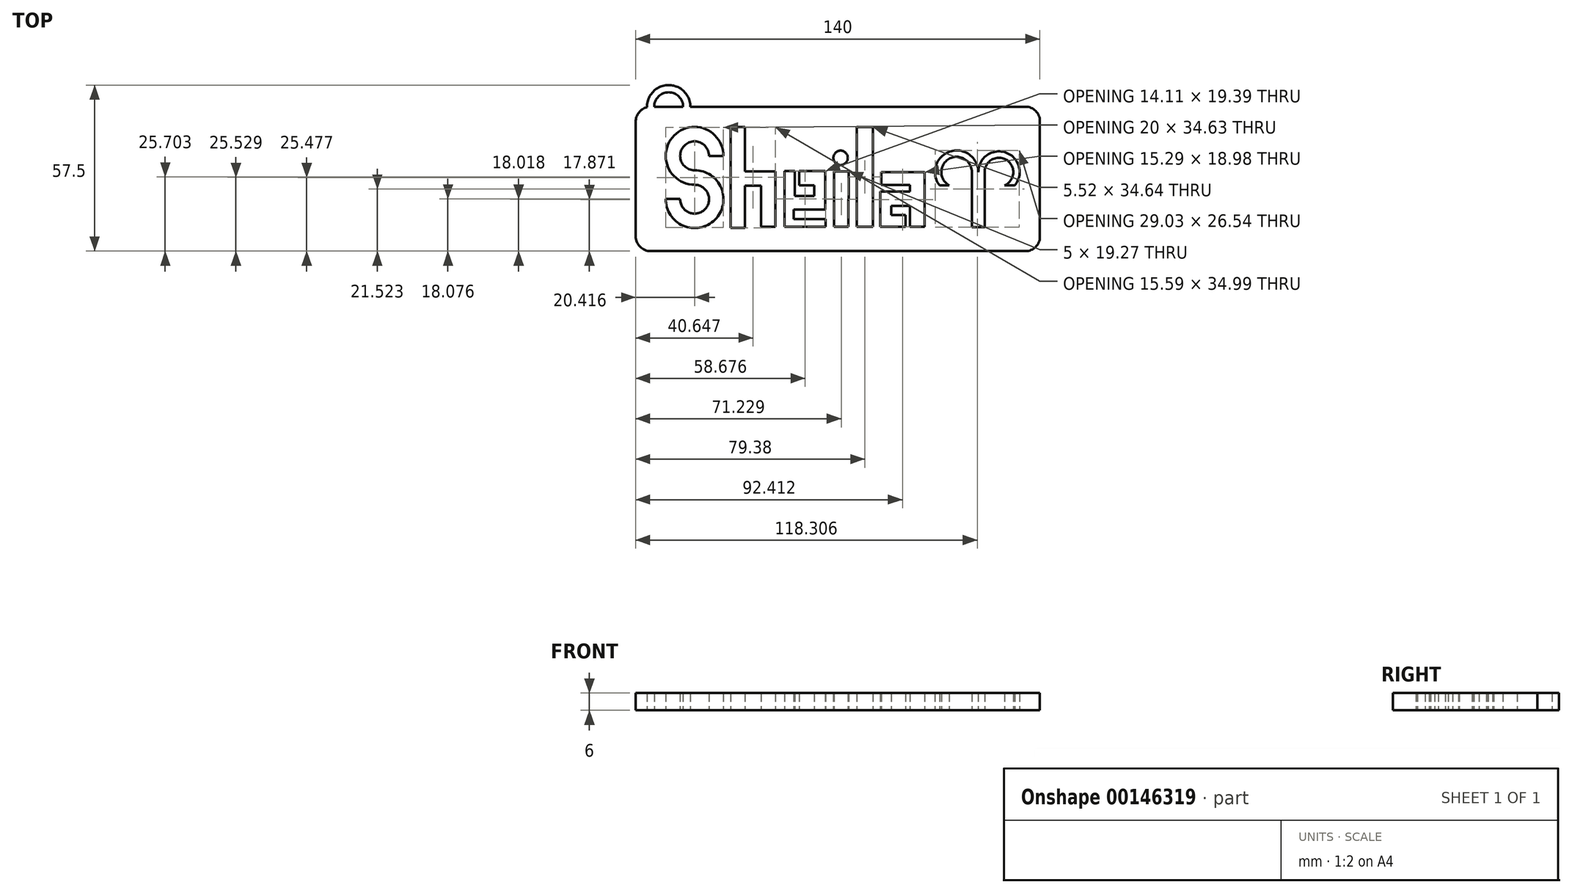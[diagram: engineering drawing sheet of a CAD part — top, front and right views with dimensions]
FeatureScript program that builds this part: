
annotation { "Feature Type Name" : "Feature", "Feature Type Description" : "" }
export const myFeature = defineFeature(function(context is Context, id is Id, definition is map)
    precondition{}
    {
        {
            var Q0;
            Q0=qCreatedBy(makeId("Top.planeOp"),FACE);
            var sketch = newSketch(context, id + "F0", { "sketchPlane" : qUnion([Q0])});
            skLineSegment(sketch, "E0.bottom", {"start": v(-68.38, 27.23) * mm, "end": v(61.38, 27.23) * mm});
            skLineSegment(sketch, "E0.top", {"start": v(-68.41, -22.77) * mm, "end": v(61.38, -22.77) * mm});
            skLineSegment(sketch, "E0.left", {"start": v(-73.62, 22) * mm, "end": v(-73.62, -17.56) * mm});
            skLineSegment(sketch, "E0.right", {"start": v(66.38, 22.23) * mm, "end": v(66.38, -17.77) * mm});
            skPoint(sketch, "E1.visualSharp", {"position": v(-73.62, 27.23) * mm});
            skArc(sketch, "E1.filletArc", {"start": v(-68.38, 27.23) * mm, "mid": v(-72.08, 25.7) * mm, "end": v(-73.62, 22) * mm});
            skPoint(sketch, "E2.visualSharp", {"position": v(-73.62, -22.77) * mm});
            skArc(sketch, "E2.filletArc", {"start": v(-73.62, -17.56) * mm, "mid": v(-72.1, -21.25) * mm, "end": v(-68.41, -22.77) * mm});
            skPoint(sketch, "E3.visualSharp", {"position": v(66.38, 27.23) * mm});
            skArc(sketch, "E3.filletArc", {"start": v(66.38, 22.23) * mm, "mid": v(64.92, 25.76) * mm, "end": v(61.38, 27.23) * mm});
            skPoint(sketch, "E4.visualSharp", {"position": v(66.38, -22.77) * mm});
            skArc(sketch, "E4.filletArc", {"start": v(61.38, -22.77) * mm, "mid": v(64.92, -21.3) * mm, "end": v(66.38, -17.77) * mm});
            skLineSegment(sketch, "E5", {"start": v(-58.07, -4.63) * mm, "end": v(-58.2, -4.63) * mm});
            skLineSegment(sketch, "E6", {"start": v(-40.77, 20.25) * mm, "end": v(-40.77, -14.74) * mm});
            skLineSegment(sketch, "E7.trimOffspring", {"start": v(-22, -14.39) * mm, "end": v(-7.9, -14.39) * mm});
            skLineSegment(sketch, "E8", {"start": v(-40.77, -14.74) * mm, "end": v(-35.77, -14.74) * mm});
            skLineSegment(sketch, "E9", {"start": v(-35.77, -14.74) * mm, "end": v(-35.77, -0.15) * mm});
            skLineSegment(sketch, "E10", {"start": v(-35.77, -0.15) * mm, "end": v(-30.2, -0.15) * mm});
            skLineSegment(sketch, "E11", {"start": v(-30.2, -0.15) * mm, "end": v(-30.2, -14.39) * mm});
            skLineSegment(sketch, "E12", {"start": v(-30.2, -14.39) * mm, "end": v(-25.18, -14.39) * mm});
            skLineSegment(sketch, "E13", {"start": v(-40.77, 20.25) * mm, "end": v(-35.77, 20.25) * mm});
            skLineSegment(sketch, "E14", {"start": v(-7.94, 5) * mm, "end": v(-22, 5) * mm});
            skLineSegment(sketch, "E15", {"start": v(-22, 5) * mm, "end": v(-22, -14.39) * mm});
            skLineSegment(sketch, "E16", {"start": v(-25.18, -14.39) * mm, "end": v(-25.18, 5.19) * mm});
            skLineSegment(sketch, "E17", {"start": v(-25.18, 4.88) * mm, "end": v(-35.77, 4.88) * mm});
            skLineSegment(sketch, "E18", {"start": v(-35.77, 4.88) * mm, "end": v(-35.77, 20.25) * mm});
            skLineSegment(sketch, "E19", {"start": v(-7.94, 5) * mm, "end": v(-7.94, -8.38) * mm});
            skLineSegment(sketch, "E20", {"start": v(-7.9, -14.39) * mm, "end": v(-7.9, -11.6) * mm});
            skLineSegment(sketch, "E21", {"start": v(-7.9, -11.6) * mm, "end": v(-18.85, -11.6) * mm});
            skLineSegment(sketch, "E22", {"start": v(-18.85, -11.6) * mm, "end": v(-18.85, -8.38) * mm});
            skLineSegment(sketch, "E23", {"start": v(-18.85, -8.38) * mm, "end": v(-7.94, -8.38) * mm});
            skLineSegment(sketch, "E24", {"start": v(-11.73, 0) * mm, "end": v(-11.73, -3.67) * mm});
            skLineSegment(sketch, "E25", {"start": v(-11.73, -3.67) * mm, "end": v(-18.48, -3.67) * mm});
            skLineSegment(sketch, "E26", {"start": v(-18.48, -3.67) * mm, "end": v(-18.48, 0) * mm});
            skLineSegment(sketch, "E27", {"start": v(-18.48, 0) * mm, "end": v(-11.73, 0) * mm});
            skLineSegment(sketch, "E28", {"start": v(-35.77, 4.88) * mm, "end": v(-25.18, 4.88) * mm});
            skLineSegment(sketch, "E29", {"start": v(-4.9, -14.39) * mm, "end": v(-4.9, 4.88) * mm});
            skLineSegment(sketch, "E30", {"start": v(-4.9, 4.88) * mm, "end": v(0.1, 4.87) * mm});
            skLineSegment(sketch, "E31", {"start": v(0.1, 4.87) * mm, "end": v(0, -14.39) * mm});
            skLineSegment(sketch, "E32", {"start": v(0, -14.39) * mm, "end": v(-4.9, -14.39) * mm});
            skLineSegment(sketch, "E33.trimOffspring", {"start": v(-4.9, -14.39) * mm, "end": v(0, -14.39) * mm});
            skCircle(sketch, "E34", {"center": v(-2.64, 9.53) * mm, "radius": 2.5 * mm});
            skLineSegment(sketch, "E35", {"start": v(3, 20.25) * mm, "end": v(3, -14.39) * mm});
            skLineSegment(sketch, "E36", {"start": v(3, -14.39) * mm, "end": v(8.52, -14.39) * mm});
            skLineSegment(sketch, "E37", {"start": v(8.52, -14.39) * mm, "end": v(8.52, 20.25) * mm});
            skLineSegment(sketch, "E38.trimOffspring", {"start": v(11.15, -14.39) * mm, "end": v(26.44, -14.39) * mm});
            skLineSegment(sketch, "E39", {"start": v(26.38, 4.6) * mm, "end": v(26.44, 4.6) * mm});
            skLineSegment(sketch, "E40", {"start": v(11.15, -14.39) * mm, "end": v(11.15, -2.12) * mm});
            skLineSegment(sketch, "E41", {"start": v(11.15, -2.12) * mm, "end": v(21.4, -2.12) * mm});
            skLineSegment(sketch, "E42", {"start": v(26.44, 4.6) * mm, "end": v(11.42, 4.6) * mm});
            skLineSegment(sketch, "E43", {"start": v(11.42, 4.6) * mm, "end": v(11.42, 0.12) * mm});
            skLineSegment(sketch, "E44", {"start": v(11.42, 0.12) * mm, "end": v(21.4, 0.12) * mm});
            skLineSegment(sketch, "E45", {"start": v(21.4, 0.12) * mm, "end": v(21.4, -2.2) * mm});
            skLineSegment(sketch, "E46", {"start": v(14.95, -7.12) * mm, "end": v(21.4, -7.12) * mm});
            skLineSegment(sketch, "E47", {"start": v(21.4, -7.12) * mm, "end": v(21.4, -10.27) * mm});
            skLineSegment(sketch, "E48", {"start": v(21.4, -10.27) * mm, "end": v(14.95, -10.27) * mm});
            skLineSegment(sketch, "E49", {"start": v(14.95, -10.27) * mm, "end": v(14.95, -7.12) * mm});
            skLineSegment(sketch, "E50", {"start": v(26.44, 4.6) * mm, "end": v(26.44, -14.39) * mm});
            skLineSegment(sketch, "E51", {"start": v(3, 20.25) * mm, "end": v(8.52, 20.25) * mm});
            skLineSegment(sketch, "E52.bottom", {"start": v(-65.84, 22.23) * mm, "end": v(58.88, 22.23) * mm});
            skLineSegment(sketch, "E52.top", {"start": v(-65.84, -17.77) * mm, "end": v(58.88, -17.77) * mm});
            skLineSegment(sketch, "E52.left", {"start": v(-68.34, 19.73) * mm, "end": v(-68.34, -15.27) * mm});
            skLineSegment(sketch, "E52.right", {"start": v(61.38, 19.73) * mm, "end": v(61.38, -15.27) * mm});
            skPoint(sketch, "E53.oppositeSnap0", {"position": v(-68.34, 2.23) * mm});
            skArc(sketch, "E54.filletArc", {"start": v(61.38, 19.73) * mm, "mid": v(60.65, 21.5) * mm, "end": v(58.88, 22.23) * mm});
            skArc(sketch, "E55.filletArc", {"start": v(58.88, -17.77) * mm, "mid": v(60.65, -17.04) * mm, "end": v(61.38, -15.27) * mm});
            skArc(sketch, "E56.filletArc", {"start": v(-65.84, 22.23) * mm, "mid": v(-67.6, 21.5) * mm, "end": v(-68.34, 19.73) * mm});
            skArc(sketch, "E57.filletArc", {"start": v(-68.34, -15.27) * mm, "mid": v(-67.6, -17.04) * mm, "end": v(-65.84, -17.77) * mm});
            skLineSegment(sketch, "E58.top", {"start": v(42.82, -14.52) * mm, "end": v(47.23, -14.52) * mm});
            skLineSegment(sketch, "E58.left", {"start": v(42.82, 4.6) * mm, "end": v(42.82, -14.52) * mm});
            skLineSegment(sketch, "E58.right", {"start": v(47.23, 4.6) * mm, "end": v(47.23, -14.52) * mm});
            skArc(sketch, "E59", {"start": v(45.04, 4.6) * mm, "mid": v(35.1, 11.7) * mm, "end": v(31.62, 0) * mm});
            skArc(sketch, "E60", {"start": v(42.82, 4.6) * mm, "mid": v(34.88, 9.16) * mm, "end": v(34.95, 0) * mm});
            skArc(sketch, "E61", {"start": v(54.09, 0) * mm, "mid": v(54.98, 8.73) * mm, "end": v(47.23, 4.6) * mm});
            skArc(sketch, "E62", {"start": v(57.7, 0) * mm, "mid": v(54.66, 11.34) * mm, "end": v(45.04, 4.6) * mm});
            skLineSegment(sketch, "E63", {"start": v(54.09, 0) * mm, "end": v(57.7, 0) * mm});
            skLineSegment(sketch, "E64", {"start": v(31.62, 0) * mm, "end": v(34.95, 0) * mm});
            skLineSegment(sketch, "E65.trimOffspring", {"start": v(-22, 4.88) * mm, "end": v(-7.94, 4.88) * mm});
            skArc(sketch, "E66", {"start": v(-54.68, 27.23) * mm, "mid": v(-62.26, 34.73) * mm, "end": v(-69.68, 27.07) * mm});
            skArc(sketch, "E67", {"start": v(-57.18, 27.23) * mm, "mid": v(-62.18, 32.23) * mm, "end": v(-67.18, 27.23) * mm});
            skLineSegment(sketch, "E68.bottom", {"start": v(-68.62, -22.77) * mm, "end": v(61.38, -22.77) * mm});
            skLineSegment(sketch, "E68.top", {"start": v(-68.62, 27.23) * mm, "end": v(61.38, 27.23) * mm});
            skLineSegment(sketch, "E68.left", {"start": v(-73.62, -17.77) * mm, "end": v(-73.62, 22.23) * mm});
            skLineSegment(sketch, "E68.right", {"start": v(66.38, -17.77) * mm, "end": v(66.38, 22.23) * mm});
            skArc(sketch, "E69.filletArc", {"start": v(-73.62, -17.77) * mm, "mid": v(-72.15, -21.3) * mm, "end": v(-68.62, -22.77) * mm});
            skArc(sketch, "E70.filletArc", {"start": v(-68.62, 27.23) * mm, "mid": v(-72.15, 25.76) * mm, "end": v(-73.62, 22.23) * mm});
            skArc(sketch, "E71", {"start": v(-43.2, 10.22) * mm, "mid": v(-60.28, 17.29) * mm, "end": v(-53.2, 0.22) * mm});
            skArc(sketch, "E72", {"start": v(-48.2, 10.22) * mm, "mid": v(-56.74, 13.75) * mm, "end": v(-53.2, 5.22) * mm});
            skArc(sketch, "E73", {"start": v(-58.2, -4.63) * mm, "mid": v(-49.72, -8.37) * mm, "end": v(-53.2, 0.22) * mm});
            skArc(sketch, "E74", {"start": v(-63.2, -4.63) * mm, "mid": v(-46.19, -11.9) * mm, "end": v(-53.2, 5.22) * mm});
            skLineSegment(sketch, "E75", {"start": v(-58.07, -4.63) * mm, "end": v(-63.2, -4.63) * mm});
            skLineSegment(sketch, "E76", {"start": v(-48.2, 10.22) * mm, "end": v(-43.2, 10.22) * mm});
            skLineSegment(sketch, "E77", {"start": v(-18.48, 0) * mm, "end": v(-18.48, 5) * mm});
            skLineSegment(sketch, "E78", {"start": v(-16.98, 0) * mm, "end": v(-16.98, 5) * mm});
            skLineSegment(sketch, "E79", {"start": v(21.4, -10.27) * mm, "end": v(21.4, -14.39) * mm});
            skLineSegment(sketch, "E80", {"start": v(21.4, -14.39) * mm, "end": v(19.9, -14.39) * mm});
            skLineSegment(sketch, "E81", {"start": v(19.9, -14.39) * mm, "end": v(19.9, -10.27) * mm});
            skSolve(sketch);
        }
        {
            var Q0;
            {var subQ0=sQuery(id+"F0.wireOp",EDGE,"E77");var subQ1=sQuery(id+"F0.wireOp",EDGE,"E14");var subQ2=makeQuery(id+"F0.imprint","INTERSECT",VERTEX,{"derivedFrom":[subQ1,subQ0]});Q0=makeQuery(id+"F0.imprint","IMPRINT",FACE,{"disambiguationData":[TD([[makeQuery(id+"F0.imprint","IMPRINT",EDGE,{"disambiguationData":[TD([[subQ2,1.0]])],"derivedFrom":subQ1}),1.0]])]});}
            var Q1;
            {var subQ0=sQuery(id+"F0.wireOp",EDGE,"E77");var subQ5=sQuery(id+"F0.wireOp",EDGE,"E65.trimOffspring");var subQ6=makeQuery(id+"F0.imprint","INTERSECT",VERTEX,{"derivedFrom":[subQ5,subQ0]});Q1=makeQuery(id+"F0.imprint","IMPRINT",FACE,{"disambiguationData":[TD([[makeQuery(id+"F0.imprint","IMPRINT",EDGE,{"disambiguationData":[TD([[subQ6,-1.0]])],"derivedFrom":subQ5}),-1.0]])]});}
            var Q2;
            Q2=makeQuery(id+"F0.imprint","IMPRINT",FACE,{"disambiguationData":[TD([[makeQuery(id+"F0.imprint","IMPRINT",EDGE,{"derivedFrom":sQuery(id+"F0.wireOp",EDGE,"E6")}),-1.0]])]});
            var Q3;
            {var subQ1=sQuery(id+"F0.wireOp",EDGE,"E2.filletArc");Q3=makeQuery(id+"F0.imprint","IMPRINT",FACE,{"disambiguationData":[TD([[makeQuery(id+"F0.imprint","IMPRINT",EDGE,{"derivedFrom":subQ1}),1.0]])]});}
            var Q4;
            {var subQ2=sQuery(id+"F0.wireOp",EDGE,"E67");Q4=makeQuery(id+"F0.imprint","IMPRINT",FACE,{"disambiguationData":[TD([[makeQuery(id+"F0.imprint","IMPRINT",EDGE,{"derivedFrom":subQ2}),-1.0]])]});}
            var Q5;
            {var subQ3=sQuery(id+"F0.wireOp",EDGE,"E24");Q5=makeQuery(id+"F0.imprint","IMPRINT",FACE,{"disambiguationData":[TD([[makeQuery(id+"F0.imprint","IMPRINT",EDGE,{"derivedFrom":subQ3}),-1.0]])]});}
            var Q6;
            Q6=makeQuery(id+"F0.imprint","IMPRINT",FACE,{"disambiguationData":[TD([[makeQuery(id+"F0.imprint","IMPRINT",EDGE,{"derivedFrom":sQuery(id+"F0.wireOp",EDGE,"E46")}),-1.0]])]});
            var Q7;
            {var subQ0=sQuery(id+"F0.wireOp",EDGE,"GSgwx7yS-cQBB-QJ6O-z8F3-R5YhPPveh4S4");Q7=makeQuery(id+"F0.imprint","IMPRINT",FACE,{"disambiguationData":[TD([[makeQuery(id+"F0.imprint","IMPRINT",EDGE,{"derivedFrom":subQ0}),-1.0]])]});}
            var Q8;
            {var subQ0=sQuery(id+"F0.wireOp",EDGE,"E79");Q8=makeQuery(id+"F0.imprint","IMPRINT",FACE,{"disambiguationData":[TD([[makeQuery(id+"F0.imprint","IMPRINT",EDGE,{"derivedFrom":subQ0}),-1.0]])]});}
            var Q9;
            {var subQ0=sQuery(id+"F0.wireOp",EDGE,"E68.top");var subQ1=sQuery(id+"F0.wireOp",EDGE,"E1.filletArc");var subQ2=makeQuery(id+"F0.imprint","INTERSECT",VERTEX,{"derivedFrom":[subQ1,subQ0]});Q9=makeQuery(id+"F0.imprint","IMPRINT",FACE,{"disambiguationData":[TD([[makeQuery(id+"F0.imprint","IMPRINT",EDGE,{"disambiguationData":[TD([[subQ2,-1.0]])],"derivedFrom":subQ1}),-1.0]])]});}
            extrude(context, id + "F1", {"entities" : qUnion([Q0, Q1, Q2, Q3, Q4, Q5, Q6, Q7, Q8, Q9]), "depth" : 6 * mm});
        }
    });
